FCSTD DOCUMENT  (FreeCAD 0.21R33694 (Git))
Label: enclosure
License: All rights reserved
LicenseURL: http://en.wikipedia.org/wiki/All_rights_reserved
objects: Part::Feature×45, App::Link×17, App::Part×6, PartDesign::CoordinateSystem×1, Sketcher::SketchObject×1, App::DocumentObjectGroup×1
note: 47 computed .brp shape members not serialized (recipe doc carries the construction recipe); baked Part::Feature solids carry a one-line shape summary decoded from their .brp

FEATURE [PartDesign::CoordinateSystem] Local_CS_4743
  AttacherType = Attacher::AttachEngine3D
  MapMode = 2
  Support = -> [X_Axis001]
FEATURE [Part::Feature] Pcb_4743
  shape: bbox 160.8 x 51.31 x 1.6 mm, 62 faces (baked)
FEATURE [Sketcher::SketchObject] PCB_Sketch_4743
  FullyConstrained = false
  sketch-geometry (4):
    g0: LineSegment StartX=69.596 StartY=-53.848 StartZ=0 EndX=230.378 EndY=-53.848 EndZ=0
    g1: LineSegment StartX=230.378 StartY=-53.848 StartZ=0 EndX=230.378 EndY=-105.156 EndZ=0
    g2: LineSegment StartX=230.378 StartY=-105.156 StartZ=0 EndX=69.596 EndY=-105.156 EndZ=0
    g3: LineSegment StartX=69.596 StartY=-105.156 StartZ=0 EndX=69.596 EndY=-53.848 EndZ=0
  constraints (4):
    c: Coincident(g2,g3)
    c: Coincident(g0,g3)
    c: Coincident(g1,g2)
    c: Coincident(g0,g1)
FEATURE [App::Part] Board_Geoms_4743
  Group = -> [Pcb_4743,PCB_Sketch_4743]
  Origin = -> Origin
FEATURE [Part::Feature] Shape  label="R8_R_0805_2012Metric_542de8cd5894"
  Placement = pos=(195.684,-81.235,0) rot=(0,0,1;3.14159rad)
  shape: bbox 2 x 1.2 x 0.45 mm, 26 faces (baked)
FEATURE [Part::Feature] Shape001  label="D4_LED_0805_2012Metric_c15a0e7d9ebd"
  Placement = pos=(130.21,-81.235,0) rot=(0,0,1;0rad)
  shape: bbox 2 x 1.25 x 1.1 mm, 50 faces (baked)
FEATURE [App::Link] D4_LED_0805_2012Metric_c15a0e7d9ebd_ln_  label="D8_LED_0805_2012Metric_47b09096554b"
  LinkPlacement = pos=(191.274,-81.235,0) rot=(0,0,1;0rad)
  LinkedObject = -> Shape001
  Placement = pos=(191.274,-81.235,0) rot=(0,0,1;0rad)
FEATURE [Part::Feature] Arduino_Nano_WithMountingHoles
  shape: bbox 43.59 x 4.635 x 18 mm, 378 faces, 0 solids (baked)
FEATURE [Part::Feature] Arduino_Nano_WithMountingHoles001
  Placement = pos=(-1.143,1.6,-7.62) rot=(0,0,1;0rad)
  shape: bbox 5 x 11.75 x 2.54 mm, 46 faces, 0 solids (baked)
FEATURE [Part::Feature] Arduino_Nano_WithMountingHoles002
  Placement = pos=(-1.143,1.6,-5.08) rot=(0,0,1;0rad)
  shape: bbox 5 x 11.75 x 2.54 mm, 46 faces, 0 solids (baked)
FEATURE [Part::Feature] Arduino_Nano_WithMountingHoles003
  Placement = pos=(-1.143,1.6,-10.16) rot=(0,0,1;0rad)
  shape: bbox 5 x 11.75 x 2.54 mm, 46 faces, 0 solids (baked)
FEATURE [Part::Feature] Arduino_Nano_WithMountingHoles004
  Placement = pos=(0,0,0) rot=(0.707107,0,0.707107;3.14159rad)
  shape: bbox 38.1 x 11.75 x 2.54 mm, 364 faces, 0 solids (baked)
FEATURE [Part::Feature] Arduino_Nano_WithMountingHoles005
  Placement = pos=(0,0,-15.24) rot=(0.707107,0,0.707107;3.14159rad)
  shape: bbox 38.1 x 11.75 x 2.54 mm, 364 faces, 0 solids (baked)
FEATURE [Part::Feature] Arduino_Nano_WithMountingHoles006
  Placement = pos=(23.85,1.75,-7.62) rot=(0,1,0;3.92699rad)
  shape: bbox 11.38 x 1.1 x 11.38 mm, 1867 faces, 0 solids (baked)
FEATURE [Part::Feature] Arduino_Nano_WithMountingHoles007
  Placement = pos=(29.05,0,-7.67) rot=(0.707107,0,-0.707107;3.14159rad)
  shape: bbox 10.32 x 1.9 x 9.71 mm, 717 faces, 0 solids (baked)
FEATURE [Part::Feature] Arduino_Nano_WithMountingHoles008
  Placement = pos=(21.86,0,-5.8) rot=(0.707107,0,-0.707107;3.14159rad)
  shape: bbox 3.8 x 0.6 x 1.7 mm, 74 faces, 0 solids (baked)
FEATURE [Part::Feature] Arduino_Nano_WithMountingHoles009
  Placement = pos=(21.86,0,-9) rot=(0.707107,0,-0.707107;3.14159rad)
  shape: bbox 3.8 x 0.6 x 1.7 mm, 74 faces, 0 solids (baked)
FEATURE [Part::Feature] Arduino_Nano_WithMountingHoles010
  Placement = pos=(36.75,0,-7.6) rot=(0.707107,0,-0.707107;3.14159rad)
  shape: bbox 3.8 x 0.6 x 1.7 mm, 74 faces, 0 solids (baked)
FEATURE [Part::Feature] Arduino_Nano_WithMountingHoles011
  Placement = pos=(36.75,0,-12) rot=(0.707107,0,-0.707107;3.14159rad)
  shape: bbox 3.8 x 0.6 x 1.7 mm, 74 faces, 0 solids (baked)
FEATURE [Part::Feature] Arduino_Nano_WithMountingHoles012
  Placement = pos=(8.2,0,-2.6) rot=(0.707107,0,-0.707107;3.14159rad)
  shape: bbox 3.8 x 0.6 x 1.7 mm, 74 faces, 0 solids (baked)
FEATURE [Part::Feature] Arduino_Nano_WithMountingHoles013
  Placement = pos=(10.4,1.6,-2.8) rot=(0,0,1;0rad)
  shape: bbox 5.518 x 1.649 x 1.609 mm, 57 faces, 0 solids (baked)
FEATURE [Part::Feature] Arduino_Nano_WithMountingHoles014
  Placement = pos=(10.4,1.6,-5.55) rot=(0,0,1;0rad)
  shape: bbox 5.518 x 1.649 x 1.609 mm, 57 faces, 0 solids (baked)
FEATURE [Part::Feature] Arduino_Nano_WithMountingHoles015
  Placement = pos=(10.4,1.6,-12.5) rot=(0,0,1;0rad)
  shape: bbox 5.518 x 1.649 x 1.609 mm, 57 faces, 0 solids (baked)
FEATURE [Part::Feature] Arduino_Nano_WithMountingHoles016
  Placement = pos=(10.4,1.6,-9.05) rot=(0,0,1;0rad)
  shape: bbox 5.518 x 1.649 x 1.609 mm, 57 faces, 0 solids (baked)
FEATURE [Part::Feature] Arduino_Nano_WithMountingHoles017
  Placement = pos=(18.5113,1.6,-3.55414) rot=(0,-1,0;0.785398rad)
  shape: bbox 3.818 x 0.8 x 3.818 mm, 71 faces, 0 solids (baked)
FEATURE [Part::Feature] Arduino_Nano_WithMountingHoles018
  Placement = pos=(38.98,1.65,-7.62) rot=(0,-1,0;1.5708rad)
  shape: bbox 9.474 x 3.821 x 11.03 mm, 243 faces, 0 solids (baked)
FEATURE [Part::Feature] Arduino_Nano_WithMountingHoles019
  Placement = pos=(32.28,1.65,-7.62) rot=(0,1,0;1.5708rad)
  shape: bbox 8.2 x 4.5 x 7.7 mm, 127 faces, 0 solids (baked)
FEATURE [Part::Feature] Arduino_Nano_WithMountingHoles020 .. Arduino_Nano_WithMountingHoles024  x5 (patterned run collapsed; names and placements below)
  shape: bbox 9.422 x 2.565 x 0.5 mm, 31 faces, 0 solids (baked)
  placements: 5 in arithmetic series — first pos=(33.28,1.65,-9.22) rot=(0,1,0;1.5708rad), step (0,0,0.8), last pos=(33.28,1.65,-6.02) rot=(0,1,0;1.5708rad)
FEATURE [Part::Feature] Arduino_Nano_WithMountingHoles025
  Placement = pos=(37.2,0,-3.3) rot=(0.707107,0,0.707107;3.14159rad)
  shape: bbox 4 x 1.81 x 1.7 mm, 124 faces, 0 solids (baked)
FEATURE [Part::Feature] Arduino_Nano_WithMountingHoles026
  Placement = pos=(7.9,0,-5.6) rot=(0.707107,0,-0.707107;3.14159rad)
  shape: bbox 4 x 1.81 x 1.7 mm, 124 faces, 0 solids (baked)
FEATURE [Part::Feature] Arduino_Nano_WithMountingHoles027
  Placement = pos=(15.25,1.6,-8.05) rot=(0,1,0;1.5708rad)
  shape: bbox 2.8 x 2.156 x 5.2 mm, 77 faces, 0 solids (baked)
FEATURE [Part::Feature] Arduino_Nano_WithMountingHoles028
  Placement = pos=(15.25,3.25,-8.05) rot=(0,0,1;0rad)
  shape: bbox 3.003 x 1.653 x 4.003 mm, 100 faces, 0 solids (baked)
FEATURE [Part::Feature] Arduino_Nano_WithMountingHoles029
  Placement = pos=(6.1,0,-10.16) rot=(0.707107,0,-0.707107;3.14159rad)
  shape: bbox 8.3 x 1.69 x 6.5 mm, 198 faces, 0 solids (baked)
FEATURE [Part::Feature] Arduino_Nano_WithMountingHoles030
  Placement = pos=(11.43,0,-4.2) rot=(0.707107,0,0.707107;3.14159rad)
  shape: bbox 1.7 x 1.384 x 4.916 mm, 85 faces, 0 solids (baked)
FEATURE [Part::Feature] Arduino_Nano_WithMountingHoles031
  Placement = pos=(15.75,0,-10.85) rot=(0.707107,0,0.707107;3.14159rad)
  shape: bbox 3 x 0.5241 x 3.2 mm, 288 faces, 0 solids (baked)
FEATURE [Part::Feature] Arduino_Nano_WithMountingHoles032
  Placement = pos=(15.75,0,-5.2) rot=(0.707107,0,0.707107;3.14159rad)
  shape: bbox 3 x 0.5241 x 3.2 mm, 277 faces, 0 solids (baked)
FEATURE [App::Part] Arduino_Nano_WithMountingHoles033  label="A1_Arduino_Nano_WithMountingHoles033_add46494fcf4"
  Group = -> [Arduino_Nano_WithMountingHoles,Arduino_Nano_WithMountingHoles001,Arduino_Nano_WithMountingHoles002,Arduino_Nano_WithMountingHoles003,Arduino_Nano_WithMountingHoles004,Arduino_Nano_WithMountingHoles005,Arduino_Nano_WithMountingHoles006,Arduino_Nano_WithMountingHoles007,Arduino_Nano_WithMountingHoles008,Arduino_Nano_WithMountingHoles009,Arduino_Nano_WithMountingHoles010,+22 more]
  Origin = -> Origin008
  Placement = pos=(200.776,-54.596,-6.5) rot=(0,0,-1;1.5708rad)
FEATURE [Part::Feature] Part__Feature  label="Neutrik NC3FAH2"
  shape: bbox 1.44 x 13.29 x 15.76 mm, 58 faces (baked)
FEATURE [Part::Feature] Part__Feature001  label="Neutrik NC3FAH003"
  shape: bbox 10.2 x 7.623 x 28.18 mm, 194 faces (baked)
FEATURE [Part::Feature] Part__Feature002  label="Neutrik NC3FAH004"
  shape: bbox 6 x 16.35 x 8 mm, 28 faces (baked)
FEATURE [Part::Feature] Part__Feature003  label="Neutrik NC3FAH005"
  shape: bbox 6 x 16.35 x 8 mm, 28 faces (baked)
FEATURE [Part::Feature] Part__Feature004  label="Neutrik NC3FAH006"
  shape: bbox 6 x 12.35 x 8 mm, 24 faces (baked)
FEATURE [Part::Feature] Part__Feature005  label="Neutrik NC3FAH007"
  shape: bbox 27.2 x 27.96 x 22.65 mm, 962 faces (baked)
FEATURE [App::Part] Neutrik_NC3FAH008  label="J3_Neutrik NC3FAH008_ddd3292a21dc"
  Group = -> [Part__Feature,Part__Feature001,Part__Feature002,Part__Feature003,Part__Feature004,Part__Feature005]
  Origin = -> Origin009
  Placement = pos=(153.76,-56.85,-1.49997) rot=(1,0,0;1.5708rad)
FEATURE [App::Link] D4_LED_0805_2012Metric_c15a0e7d9ebd_ln_001  label="D6_LED_0805_2012Metric_a3d814ee4790"
  LinkPlacement = pos=(142.251,-81.235,0) rot=(0,0,1;0rad)
  LinkedObject = -> Shape001
  Placement = pos=(142.251,-81.235,0) rot=(0,0,1;0rad)
FEATURE [App::Link] R8_R_0805_2012Metric_542de8cd5894_ln_  label="R4_R_0805_2012Metric_9a44cdb4aa3b"
  LinkPlacement = pos=(115.674,-81.235,0) rot=(0,0,1;0rad)
  LinkedObject = -> Shape
  Placement = pos=(115.674,-81.235,0) rot=(0,0,1;0rad)
FEATURE [App::Link] R8_R_0805_2012Metric_542de8cd5894_ln_001  label="R5_R_0805_2012Metric_4d9526face75"
  LinkPlacement = pos=(146.812,-81.235,0) rot=(0,0,1;0rad)
  LinkedObject = -> Shape
  Placement = pos=(146.812,-81.235,0) rot=(0,0,1;0rad)
FEATURE [App::Link] D4_LED_0805_2012Metric_c15a0e7d9ebd_ln_002  label="D2_LED_0805_2012Metric_bbd0da5a3e7d"
  LinkPlacement = pos=(111.427,-81.235,0) rot=(0,0,1;0rad)
  LinkedObject = -> Shape001
  Placement = pos=(111.427,-81.235,0) rot=(0,0,1;0rad)
FEATURE [App::Link] R8_R_0805_2012Metric_542de8cd5894_ln_002  label="R2_R_0805_2012Metric_ba1683f544c3"
  LinkPlacement = pos=(103.783,-81.235,0) rot=(0,0,1;3.14159rad)
  LinkedObject = -> Shape
  Placement = pos=(103.783,-81.235,0) rot=(0,0,1;3.14159rad)
FEATURE [App::Link] R8_R_0805_2012Metric_542de8cd5894_ln_003  label="R6_R_0805_2012Metric_406797a00f78"
  LinkPlacement = pos=(177.142,-81.235,0) rot=(0,0,1;0rad)
  LinkedObject = -> Shape
  Placement = pos=(177.142,-81.235,0) rot=(0,0,1;0rad)
FEATURE [App::Link] J3_Neutrik_NC3FAH008_ddd3292a21dc_ln_  label="J1_Neutrik NC3FAH008_6e6a4ee42cfc"
  LinkPlacement = pos=(92.8,-56.85,-0.499976) rot=(1,0,0;1.5708rad)
  LinkedObject = -> Neutrik_NC3FAH008
  Placement = pos=(92.8,-56.85,-0.499976) rot=(1,0,0;1.5708rad)
FEATURE [App::Link] D4_LED_0805_2012Metric_c15a0e7d9ebd_ln_003  label="D3_LED_0805_2012Metric_1a4d4566548c"
  LinkPlacement = pos=(99.3725,-81.235,0) rot=(0,0,1;0rad)
  LinkedObject = -> Shape001
  Placement = pos=(99.3725,-81.235,0) rot=(0,0,1;0rad)
FEATURE [App::Link] D4_LED_0805_2012Metric_c15a0e7d9ebd_ln_004  label="D1_LED_0805_2012Metric_465b72bef6d4"
  LinkPlacement = pos=(81.6125,-81.235,0) rot=(0,0,1;0rad)
  LinkedObject = -> Shape001
  Placement = pos=(81.6125,-81.235,0) rot=(0,0,1;0rad)
FEATURE [App::Link] R8_R_0805_2012Metric_542de8cd5894_ln_004  label="R7_R_0805_2012Metric_9987731a8ca5"
  LinkPlacement = pos=(165.113,-81.235,0) rot=(0,0,1;3.14159rad)
  LinkedObject = -> Shape
  Placement = pos=(165.113,-81.235,0) rot=(0,0,1;3.14159rad)
FEATURE [App::Link] J3_Neutrik_NC3FAH008_ddd3292a21dc_ln_001  label="J4_Neutrik NC3FAH008_f1a8b087ef94"
  LinkPlacement = pos=(184.24,-56.85,-0.499976) rot=(1,0,0;1.5708rad)
  LinkedObject = -> Neutrik_NC3FAH008
  Placement = pos=(184.24,-56.85,-0.499976) rot=(1,0,0;1.5708rad)
FEATURE [App::Link] R8_R_0805_2012Metric_542de8cd5894_ln_005  label="R1_R_0805_2012Metric_d44ece5b64db"
  LinkPlacement = pos=(86.0225,-81.235,0) rot=(0,0,1;0rad)
  LinkedObject = -> Shape
  Placement = pos=(86.0225,-81.235,0) rot=(0,0,1;0rad)
FEATURE [App::Link] D4_LED_0805_2012Metric_c15a0e7d9ebd_ln_005  label="D7_LED_0805_2012Metric_17e1e7723463"
  LinkPlacement = pos=(172.798,-81.235,0) rot=(0,0,1;0rad)
  LinkedObject = -> Shape001
  Placement = pos=(172.798,-81.235,0) rot=(0,0,1;0rad)
FEATURE [App::Link] R8_R_0805_2012Metric_542de8cd5894_ln_006  label="R3_R_0805_2012Metric_9e949f457a33"
  LinkPlacement = pos=(134.62,-81.235,0) rot=(0,0,1;3.14159rad)
  LinkedObject = -> Shape
  Placement = pos=(134.62,-81.235,0) rot=(0,0,1;3.14159rad)
FEATURE [App::Link] J3_Neutrik_NC3FAH008_ddd3292a21dc_ln_002  label="J2_Neutrik NC3FAH008_c8d545dbce63"
  LinkPlacement = pos=(123.28,-56.85,-0.499976) rot=(1,0,0;1.5708rad)
  LinkedObject = -> Neutrik_NC3FAH008
  Placement = pos=(123.28,-56.85,-0.499976) rot=(1,0,0;1.5708rad)
FEATURE [App::Link] D4_LED_0805_2012Metric_c15a0e7d9ebd_ln_006  label="D5_LED_0805_2012Metric_2f24e8875b89"
  LinkPlacement = pos=(160.703,-81.235,0) rot=(0,0,1;0rad)
  LinkedObject = -> Shape001
  Placement = pos=(160.703,-81.235,0) rot=(0,0,1;0rad)
FEATURE [App::Part] Top_4743
  Group = -> [Shape,Shape001,D4_LED_0805_2012Metric_c15a0e7d9ebd_ln_,Arduino_Nano_WithMountingHoles033,Neutrik_NC3FAH008,D4_LED_0805_2012Metric_c15a0e7d9ebd_ln_001,R8_R_0805_2012Metric_542de8cd5894_ln_,R8_R_0805_2012Metric_542de8cd5894_ln_001,D4_LED_0805_2012Metric_c15a0e7d9ebd_ln_002,R8_R_0805_2012Metric_542de8cd5894_ln_002,R8_R_0805_2012Metric_542de8cd5894_ln_003,J3_Neutrik_NC3FAH008_ddd3292a21dc_ln_,+9 more]
  Origin = -> Origin003
FEATURE [App::Part] Step_Models_4743
  Group = -> [Top_4743]
  Origin = -> Origin002
FEATURE [App::Part] Board_4743  label="gameshow_v4"
  Group = -> [Local_CS_4743,Board_Geoms_4743,Step_Models_4743]
  Origin = -> Origin001
FEATURE [Part::Feature] FusionAxisZ1  label="Z"
  shape: bbox 0.8 x 0.8 x 14 mm, 8 faces (baked)
FEATURE [Part::Feature] FusionAxisY1  label="Y"
  Placement = pos=(0,0,0.05) rot=(1,0,0;-1.5708rad)
  shape: bbox 0.8 x 14 x 0.8 mm, 8 faces (baked)
FEATURE [Part::Feature] FusionAxisX1  label="X"
  Placement = pos=(0,-0.05,0) rot=(0,1,0;1.5708rad)
  shape: bbox 14 x 0.8 x 0.8 mm, 8 faces (baked)
FEATURE [App::DocumentObjectGroup] axis
  Group = -> [FusionAxisZ1,FusionAxisY1,FusionAxisX1]
